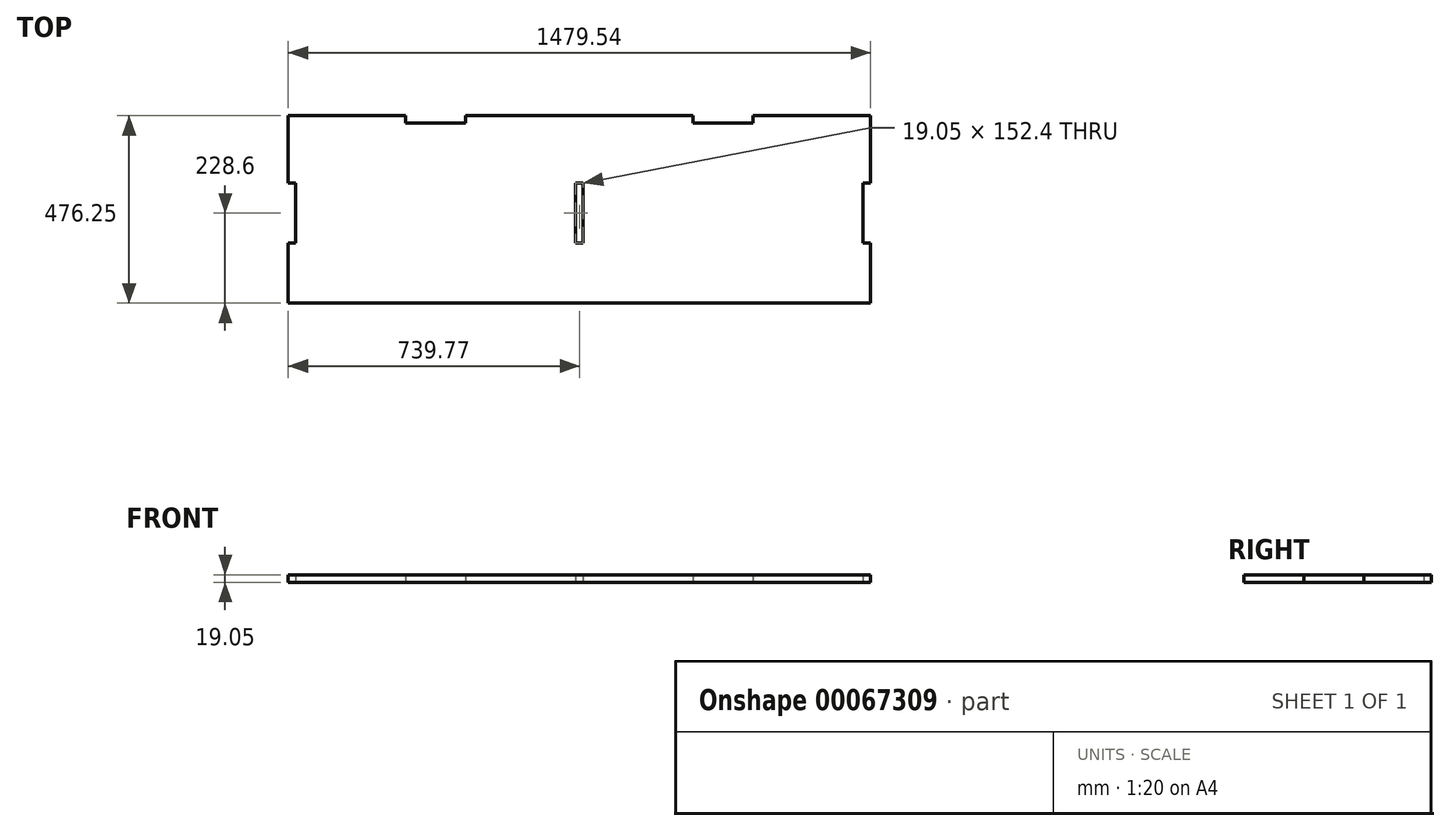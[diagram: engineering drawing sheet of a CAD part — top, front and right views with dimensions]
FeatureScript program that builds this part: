
annotation { "Feature Type Name" : "Feature", "Feature Type Description" : "" }
export const myFeature = defineFeature(function(context is Context, id is Id, definition is map)
    precondition{}
    {
        {
            var Q0;
            Q0=qCreatedBy(makeId("Top.planeOp"),FACE);
            var sketch = newSketch(context, id + "F0", { "sketchPlane" : qUnion([Q0])});
            skLineSegment(sketch, "E0.top", {"start": v(-739.78, -476.25) * mm, "end": v(739.78, -476.25) * mm});
            skLineSegment(sketch, "E0.left", {"start": v(-739.78, 0) * mm, "end": v(-739.78, -476.25) * mm});
            skLineSegment(sketch, "E0.right", {"start": v(739.78, 0) * mm, "end": v(739.77, -476.25) * mm});
            skLineSegment(sketch, "E1.bottom", {"start": v(-9.53, -171.45) * mm, "end": v(9.52, -171.45) * mm});
            skLineSegment(sketch, "E1.top", {"start": v(-9.53, -323.85) * mm, "end": v(9.52, -323.85) * mm});
            skLineSegment(sketch, "E1.left", {"start": v(-9.53, -171.45) * mm, "end": v(-9.53, -323.85) * mm});
            skLineSegment(sketch, "E1.right", {"start": v(9.52, -171.45) * mm, "end": v(9.52, -323.85) * mm});
            skLineSegment(sketch, "E2", {"start": v(-739.78, 0) * mm, "end": v(739.78, 0) * mm});
            skLineSegment(sketch, "E3.bottom", {"start": v(-441.33, 0) * mm, "end": v(-288.93, 0) * mm});
            skLineSegment(sketch, "E3.top", {"start": v(-441.33, -19.05) * mm, "end": v(-288.93, -19.05) * mm});
            skLineSegment(sketch, "E3.left", {"start": v(-441.33, 0) * mm, "end": v(-441.33, -19.05) * mm});
            skLineSegment(sketch, "E3.right", {"start": v(-288.93, 0) * mm, "end": v(-288.93, -19.05) * mm});
            skLineSegment(sketch, "E4.bottom", {"start": v(-739.78, -171.45) * mm, "end": v(-720.73, -171.45) * mm});
            skLineSegment(sketch, "E4.top", {"start": v(-739.78, -323.85) * mm, "end": v(-720.73, -323.85) * mm});
            skLineSegment(sketch, "E4.left", {"start": v(-739.78, -171.45) * mm, "end": v(-739.78, -323.85) * mm});
            skLineSegment(sketch, "E4.right", {"start": v(-720.73, -171.45) * mm, "end": v(-720.73, -323.85) * mm});
            skLineSegment(sketch, "E5.bottom", {"start": v(739.78, -171.45) * mm, "end": v(720.73, -171.45) * mm});
            skLineSegment(sketch, "E5.top", {"start": v(739.78, -323.85) * mm, "end": v(720.73, -323.85) * mm});
            skLineSegment(sketch, "E5.left", {"start": v(739.78, -171.45) * mm, "end": v(739.78, -323.85) * mm});
            skLineSegment(sketch, "E5.right", {"start": v(720.73, -171.45) * mm, "end": v(720.73, -323.85) * mm});
            skLineSegment(sketch, "E6.bottom", {"start": v(288.93, 0) * mm, "end": v(441.33, 0) * mm});
            skLineSegment(sketch, "E6.top", {"start": v(288.93, -19.05) * mm, "end": v(441.33, -19.05) * mm});
            skLineSegment(sketch, "E6.left", {"start": v(288.93, 0) * mm, "end": v(288.93, -19.05) * mm});
            skLineSegment(sketch, "E6.right", {"start": v(441.33, 0) * mm, "end": v(441.33, -19.05) * mm});
            skSolve(sketch);
        }
        {
            var Q0;
            {var subQ15=sQuery(id+"F0.wireOp",EDGE,"E0.top");Q0=makeQuery(id+"F0.imprint","IMPRINT",FACE,{"disambiguationData":[TD([[makeQuery(id+"F0.imprint","IMPRINT",EDGE,{"derivedFrom":subQ15}),1.0]])]});}
            extrude(context, id + "F1", {"entities" : qUnion([Q0]), "depth" : 19.05 * mm});
        }
    });
